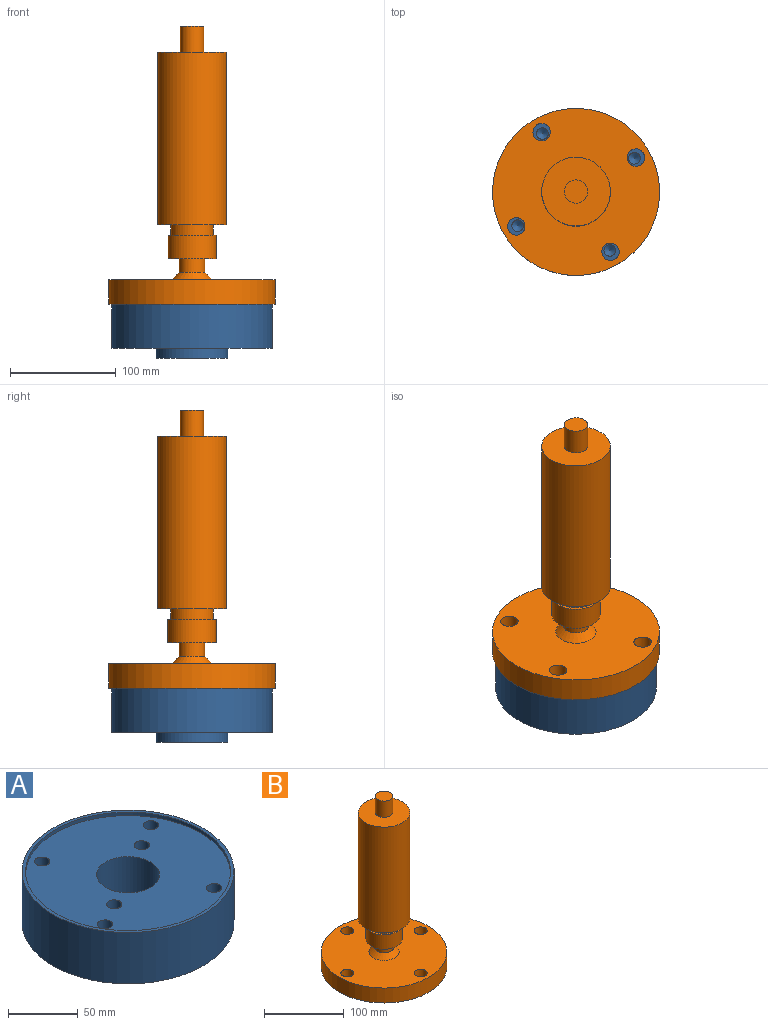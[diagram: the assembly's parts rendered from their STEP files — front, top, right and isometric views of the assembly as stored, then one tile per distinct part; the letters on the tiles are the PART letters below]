
ASSEMBLY  parts=2 mates=1
PART A: 24 faces, bbox 152x152x54 mm
  f0: cylinder r=76mm len=152mm, axis (0,0,-1), area 21488.5mm2, adj f1,f3
  f1: plane 152x152mm, normal (0,0,1), area 1174.2mm2, adj f0,f5
  f2: cylinder r=34mm len=68mm, axis (0,0,-1), area 1922.7mm2, adj f3,f4
  f3: plane 152x152mm, normal (0,0,-1), area 14514.2mm2, adj f0,f2
  f4: plane 68x68mm, normal (0,0,-1), area 3015.9mm2, adj f2,f11
  f5: cylinder r=73.5mm len=147mm, axis (0,0,1), area 1385.4mm2, adj f1,f6
  f6: plane 147x147mm, normal (0,0,1), area 14811mm2, adj f5,f7,f13,f15,f17,f19,f21,f23
  f7: cylinder r=22.5mm len=45mm, axis (0,0,1), area 5654.9mm2, adj f6,f8
  f8: plane 45x45mm, normal (0,0,1), area 205mm2, adj f7,f9
  f9: cylinder r=21mm len=42mm, axis (0,0,1), area 263.9mm2, adj f8,f10
  f10: plane 42x42mm, normal (0,0,1), area 769.7mm2, adj f9,f11
  f11: cylinder r=14mm len=28mm, axis (0,0,1), area 791.7mm2, adj f4,f10
  f12: cone r=0mm half-angle=59deg, axis (0,0,1), area 110.9mm2, adj f13
  f13: cylinder r=5.5mm len=25mm, axis (0,0,1), area 863.9mm2, adj f6,f12
  f14: cone r=0mm half-angle=59deg, axis (0,0,1), area 110.9mm2, adj f15
  f15: cylinder r=5.5mm len=25mm, axis (0,0,1), area 863.9mm2, adj f6,f14
  f16: cone r=0mm half-angle=59deg, axis (0,0,1), area 110.9mm2, adj f17
  f17: cylinder r=5.5mm len=25mm, axis (0,0,1), area 863.9mm2, adj f6,f16
  f18: cone r=0mm half-angle=59deg, axis (0,0,1), area 110.9mm2, adj f19
  f19: cylinder r=5.5mm len=25mm, axis (0,0,1), area 863.9mm2, adj f6,f18
  f20: cone r=0mm half-angle=59deg, axis (0,0,1), area 110.9mm2, adj f21
  f21: cylinder r=5.5mm len=25mm, axis (0,0,1), area 863.9mm2, adj f6,f20
  f22: cone r=0mm half-angle=59deg, axis (0,0,1), area 110.9mm2, adj f23
  f23: cylinder r=5.5mm len=25mm, axis (0,0,1), area 863.9mm2, adj f6,f22
PART B: 25 faces, bbox 158x158x268 mm
  f0: plane 84.3x84.3mm, normal (0,0,-1), area 5267.3mm2, adj f9,f12
  f1: cylinder r=8.25mm len=23mm, axis (0,0,-1), area 1192.2mm2, adj f7,f8
  f2: cylinder r=8.25mm len=23mm, axis (0,0,-1), area 1192.2mm2, adj f7,f8
  f3: cylinder r=8.25mm len=23mm, axis (0,0,-1), area 1192.2mm2, adj f7,f8
  f4: cylinder r=8.25mm len=23mm, axis (0,0,-1), area 1192.2mm2, adj f7,f8
  f5: cylinder r=5.25mm len=18.25mm, axis (0,0,-1), area 602mm2, adj f12,f14
  f6: cylinder r=79mm len=158mm, axis (0,0,-1), area 11416.5mm2, adj f7,f8
  f7: plane 158x158mm, normal (0,0,1), area 17617.3mm2, adj f1,f2,f3,f4,f6,f13
  f8: plane 158x158mm, normal (0,0,-1), area 10174.6mm2, adj f1,f2,f3,f4,f6,f10
  f9: cylinder r=42.15mm len=84.3mm, axis (0,0,1), area 1324.2mm2, adj f0,f11
  f10: cylinder r=52.25mm len=104.5mm, axis (0,0,1), area 1641.5mm2, adj f8,f11
  f11: plane 104.5x104.5mm, normal (0,0,-1), area 2995.3mm2, adj f9,f10
  f12: cone r=10mm half-angle=45deg, axis (0,0,-1), area 321.8mm2, adj f0,f5
  f13: cone r=19mm half-angle=45deg, axis (0,0,-1), area 964.1mm2, adj f7,f15
  f14: plane 10.5x10.5mm, normal (0,0,-1), area 86.6mm2, adj f5
  f15: cylinder r=12mm len=24mm, axis (0,0,-1), area 980.2mm2, adj f13,f18
  f16: cylinder r=22.75mm len=45.5mm, axis (0,0,-1), area 3144.7mm2, adj f17,f18
  f17: plane 45.5x45.5mm, normal (0,0,1), area 369.3mm2, adj f16,f19
  f18: plane 45.5x45.5mm, normal (0,0,-1), area 1173.6mm2, adj f15,f16
  f19: cylinder r=20mm len=40mm, axis (0,0,-1), area 1256.6mm2, adj f17,f22
  f20: cylinder r=32.5mm len=163mm, axis (0,0,-1), area 33285.2mm2, adj f21,f22
  f21: plane 65x65mm, normal (0,0,1), area 2938.2mm2, adj f20,f23
  f22: plane 65x65mm, normal (0,0,-1), area 2061.7mm2, adj f19,f20
  f23: cylinder r=11mm len=25mm, axis (0,0,-1), area 1727.9mm2, adj f21,f24
  f24: plane 22x22mm, normal (0,0,1), area 380.1mm2, adj f23
PLACE A at identity fixed
PLACE B rot(axis=(0,0,-1),60.1deg) t=(0,0,51)mm
MATE revolute B.f12 <-> A.f7  axis (0,0,-1) through (0,0,51)mm
